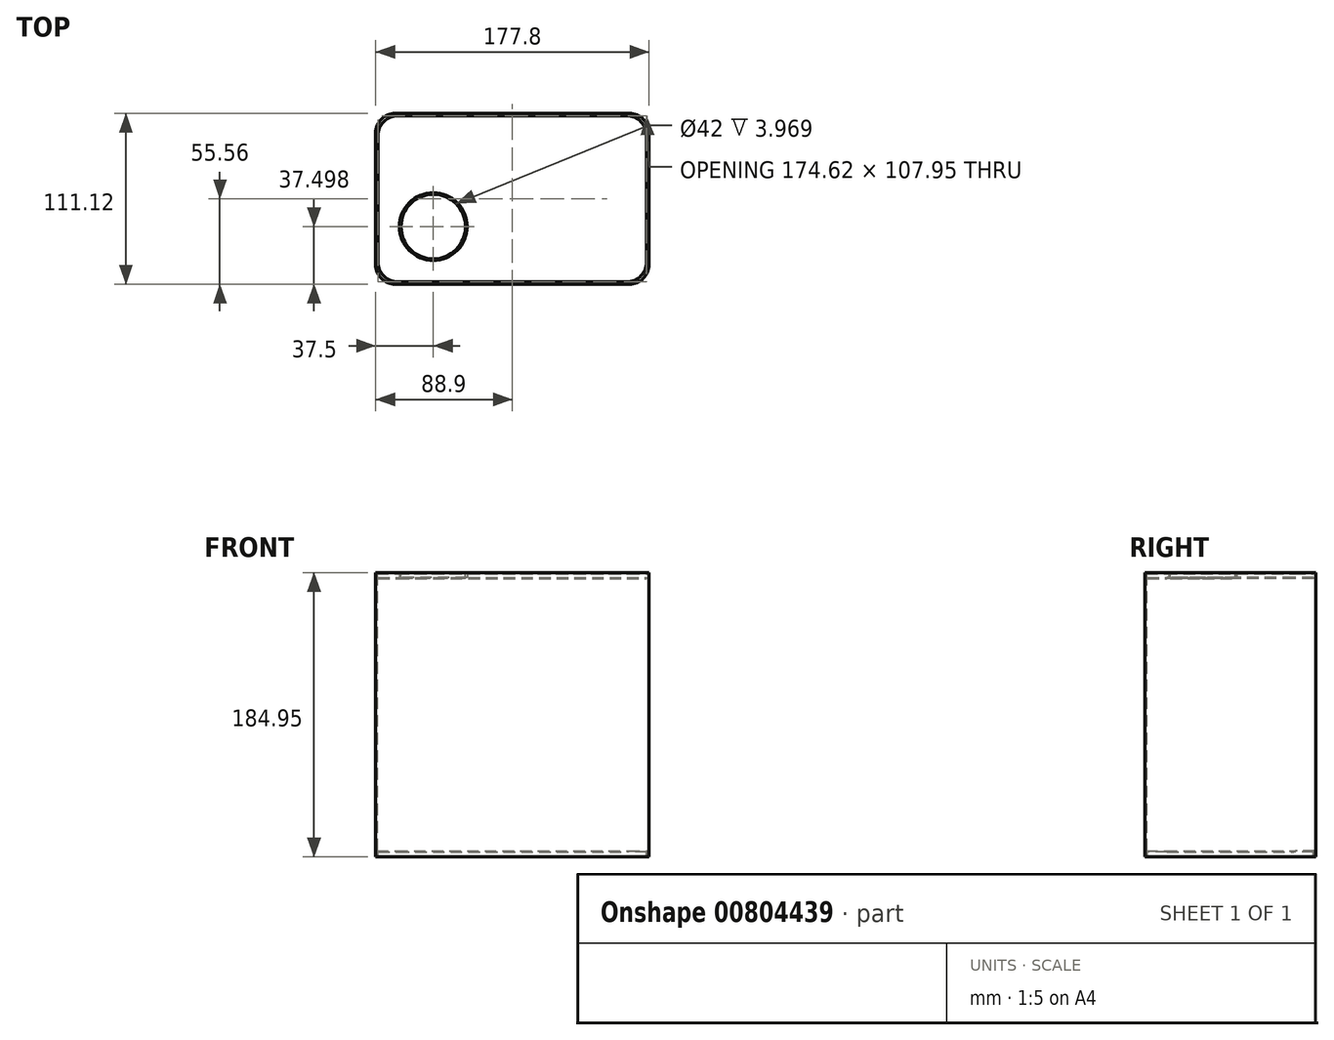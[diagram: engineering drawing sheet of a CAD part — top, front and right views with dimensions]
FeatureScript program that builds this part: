
annotation { "Feature Type Name" : "Feature", "Feature Type Description" : "" }
export const myFeature = defineFeature(function(context is Context, id is Id, definition is map)
    precondition{}
    {
        {
            var Q0;
            Q0=qCreatedBy(makeId("Top.planeOp"),FACE);
            var sketch = newSketch(context, id + "F0", { "sketchPlane" : qUnion([Q0])});
            skLineSegment(sketch, "E0.bottom", {"start": v(-76.2, -55.56) * mm, "end": v(76.2, -55.56) * mm});
            skLineSegment(sketch, "E0.top", {"start": v(-76.2, 55.56) * mm, "end": v(76.2, 55.56) * mm});
            skLineSegment(sketch, "E0.left", {"start": v(-88.9, -42.86) * mm, "end": v(-88.9, 42.86) * mm});
            skLineSegment(sketch, "E0.right", {"start": v(88.9, -42.86) * mm, "end": v(88.9, 42.86) * mm});
            skPoint(sketch, "E0.middle", {"position": v(0, 0) * mm});
            skPoint(sketch, "E1.visualSharp", {"position": v(-88.9, -55.56) * mm});
            skArc(sketch, "E1.filletArc", {"start": v(-88.9, -42.86) * mm, "mid": v(-85.18, -51.84) * mm, "end": v(-76.2, -55.56) * mm});
            skPoint(sketch, "E2.visualSharp", {"position": v(-88.9, 55.56) * mm});
            skArc(sketch, "E2.filletArc", {"start": v(-76.2, 55.56) * mm, "mid": v(-85.18, 51.84) * mm, "end": v(-88.9, 42.86) * mm});
            skPoint(sketch, "E3.visualSharp", {"position": v(88.9, 55.56) * mm});
            skArc(sketch, "E3.filletArc", {"start": v(88.9, 42.86) * mm, "mid": v(85.18, 51.84) * mm, "end": v(76.2, 55.56) * mm});
            skPoint(sketch, "E4.visualSharp", {"position": v(88.9, -55.56) * mm});
            skArc(sketch, "E4.filletArc", {"start": v(76.2, -55.56) * mm, "mid": v(85.18, -51.84) * mm, "end": v(88.9, -42.86) * mm});
            skSolve(sketch);
        }
        {
            var Q0;
            Q0 = qSketchRegion(id + "F0", true);
            extrude(context, id + "F1", {"entities" : qUnion([Q0]), "endBound" : BoundingType.SYMMETRIC, "depth" : 180.97 * mm, "offsetDistance" : 25.4 * mm});
        }
        {
            var Q0;
            Q0=makeQuery(id+"F1.opExtrude","CAP_FACE",FACE,{"disambiguationData":[OSD([sQuery(id+"F0.wireOp",EDGE,"E0.bottom"),sQuery(id+"F0.wireOp",EDGE,"E0.top"),sQuery(id+"F0.wireOp",EDGE,"E0.left"),sQuery(id+"F0.wireOp",EDGE,"E0.right"),sQuery(id+"F0.wireOp",EDGE,"E1.filletArc"),sQuery(id+"F0.wireOp",EDGE,"E2.filletArc"),sQuery(id+"F0.wireOp",EDGE,"E3.filletArc"),sQuery(id+"F0.wireOp",EDGE,"E4.filletArc")])],"isStart":false});
            var sketch = newSketch(context, id + "F2", { "sketchPlane" : qUnion([Q0])});
            skLineSegment(sketch, "E5.bottom", {"start": v(-74.61, 53.98) * mm, "end": v(74.61, 53.98) * mm});
            skLineSegment(sketch, "E5.top", {"start": v(-74.61, -53.98) * mm, "end": v(74.61, -53.98) * mm});
            skLineSegment(sketch, "E5.left", {"start": v(-87.31, 41.27) * mm, "end": v(-87.31, -41.28) * mm});
            skLineSegment(sketch, "E5.right", {"start": v(87.31, 41.28) * mm, "end": v(87.31, -41.27) * mm});
            skPoint(sketch, "E5.middle", {"position": v(0, 0) * mm});
            skPoint(sketch, "E6.visualSharp", {"position": v(-87.31, 53.98) * mm});
            skArc(sketch, "E6.filletArc", {"start": v(-74.61, 53.98) * mm, "mid": v(-83.6, 50.26) * mm, "end": v(-87.31, 41.27) * mm});
            skPoint(sketch, "E7.visualSharp", {"position": v(87.31, 53.98) * mm});
            skArc(sketch, "E7.filletArc", {"start": v(87.31, 41.28) * mm, "mid": v(83.6, 50.26) * mm, "end": v(74.61, 53.97) * mm});
            skPoint(sketch, "E8.visualSharp", {"position": v(87.31, -53.98) * mm});
            skArc(sketch, "E8.filletArc", {"start": v(74.61, -53.98) * mm, "mid": v(83.6, -50.26) * mm, "end": v(87.31, -41.27) * mm});
            skPoint(sketch, "E9.visualSharp", {"position": v(-87.31, -53.98) * mm});
            skArc(sketch, "E9.filletArc", {"start": v(-87.31, -41.28) * mm, "mid": v(-83.6, -50.26) * mm, "end": v(-74.61, -53.98) * mm});
            skSolve(sketch);
        }
        {
            var Q0;
            Q0=makeQuery(id+"F2.imprint","IMPRINT",FACE,{"disambiguationData":[TD([[makeQuery(id+"F2.imprint","IMPRINT",EDGE,{"derivedFrom":sQuery(id+"F2.wireOp",EDGE,"E5.bottom")}),-1.0]])]});
            extrude(context, id + "F3", {"entities" : qUnion([Q0]), "operationType" : NewBodyOperationType.REMOVE, "oppositeDirection" : true, "depth" : 3.17 * mm, "offsetDistance" : 25.4 * mm});
        }
        {
            var Q0;
            Q0=makeQuery(id+"F1.opExtrude","CAP_FACE",FACE,{"disambiguationData":[OSD([sQuery(id+"F0.wireOp",EDGE,"E0.bottom"),sQuery(id+"F0.wireOp",EDGE,"E0.top"),sQuery(id+"F0.wireOp",EDGE,"E0.left"),sQuery(id+"F0.wireOp",EDGE,"E0.right"),sQuery(id+"F0.wireOp",EDGE,"E1.filletArc"),sQuery(id+"F0.wireOp",EDGE,"E2.filletArc"),sQuery(id+"F0.wireOp",EDGE,"E3.filletArc"),sQuery(id+"F0.wireOp",EDGE,"E4.filletArc")])],"isStart":true});
            var sketch = newSketch(context, id + "F4", { "sketchPlane" : qUnion([Q0])});
            skLineSegment(sketch, "E10.bottom", {"start": v(-75.4, 54.77) * mm, "end": v(75.4, 54.77) * mm});
            skLineSegment(sketch, "E10.top", {"start": v(-75.4, -54.77) * mm, "end": v(75.4, -54.77) * mm});
            skLineSegment(sketch, "E10.left", {"start": v(-88.1, 42.07) * mm, "end": v(-88.1, -42.07) * mm});
            skLineSegment(sketch, "E10.right", {"start": v(88.1, 42.07) * mm, "end": v(88.1, -42.07) * mm});
            skPoint(sketch, "E10.middle", {"position": v(0, 0) * mm});
            skPoint(sketch, "E11.visualSharp", {"position": v(-88.1, 54.77) * mm});
            skArc(sketch, "E11.filletArc", {"start": v(-75.4, 54.77) * mm, "mid": v(-84.39, 51.05) * mm, "end": v(-88.1, 42.07) * mm});
            skPoint(sketch, "E12.visualSharp", {"position": v(88.1, 54.77) * mm});
            skArc(sketch, "E12.filletArc", {"start": v(88.1, 42.07) * mm, "mid": v(84.39, 51.05) * mm, "end": v(75.4, 54.77) * mm});
            skPoint(sketch, "E13.visualSharp", {"position": v(88.1, -54.77) * mm});
            skArc(sketch, "E13.filletArc", {"start": v(75.4, -54.77) * mm, "mid": v(84.39, -51.05) * mm, "end": v(88.1, -42.07) * mm});
            skPoint(sketch, "E14.visualSharp", {"position": v(-88.1, -54.77) * mm});
            skArc(sketch, "E14.filletArc", {"start": v(-88.1, -42.07) * mm, "mid": v(-84.39, -51.05) * mm, "end": v(-75.4, -54.77) * mm});
            skSolve(sketch);
        }
        {
            var Q0;
            Q0=makeQuery(id+"F4.imprint","IMPRINT",FACE,{"disambiguationData":[TD([[makeQuery(id+"F4.imprint","IMPRINT",EDGE,{"derivedFrom":sQuery(id+"F4.wireOp",EDGE,"E10.bottom")}),-1.0]])]});
            extrude(context, id + "F5", {"entities" : qUnion([Q0]), "operationType" : NewBodyOperationType.REMOVE, "endBound" : BoundingType.UP_TO_NEXT, "oppositeDirection" : true, "depth" : 25.4 * mm, "hasOffset" : true, "offsetDistance" : 0.8 * mm});
        }
        {
            var Q0;
            Q0=makeQuery(id+"F1.opExtrude","CAP_FACE",FACE,{"disambiguationData":[OSD([sQuery(id+"F0.wireOp",EDGE,"E0.bottom"),sQuery(id+"F0.wireOp",EDGE,"E0.top"),sQuery(id+"F0.wireOp",EDGE,"E0.left"),sQuery(id+"F0.wireOp",EDGE,"E0.right"),sQuery(id+"F0.wireOp",EDGE,"E1.filletArc"),sQuery(id+"F0.wireOp",EDGE,"E2.filletArc"),sQuery(id+"F0.wireOp",EDGE,"E3.filletArc"),sQuery(id+"F0.wireOp",EDGE,"E4.filletArc")])],"isStart":true});
            var sketch = newSketch(context, id + "F6", { "sketchPlane" : qUnion([Q0])});
            skLineSegment(sketch, "E15.bottom", {"start": v(-76.2, 55.56) * mm, "end": v(76.2, 55.56) * mm});
            skLineSegment(sketch, "E15.top", {"start": v(-76.2, -55.56) * mm, "end": v(76.2, -55.56) * mm});
            skLineSegment(sketch, "E15.left", {"start": v(-88.9, 42.86) * mm, "end": v(-88.9, -42.86) * mm});
            skLineSegment(sketch, "E15.right", {"start": v(88.9, 42.86) * mm, "end": v(88.9, -42.86) * mm});
            skPoint(sketch, "E15.middle", {"position": v(0, 0) * mm});
            skPoint(sketch, "E16.visualSharp", {"position": v(-88.9, 55.56) * mm});
            skArc(sketch, "E16.filletArc", {"start": v(-76.2, 55.56) * mm, "mid": v(-85.18, 51.84) * mm, "end": v(-88.9, 42.86) * mm});
            skPoint(sketch, "E17.visualSharp", {"position": v(88.9, 55.56) * mm});
            skArc(sketch, "E17.filletArc", {"start": v(88.9, 42.86) * mm, "mid": v(85.18, 51.84) * mm, "end": v(76.2, 55.56) * mm});
            skPoint(sketch, "E18.visualSharp", {"position": v(88.9, -55.56) * mm});
            skArc(sketch, "E18.filletArc", {"start": v(76.2, -55.56) * mm, "mid": v(85.18, -51.84) * mm, "end": v(88.9, -42.86) * mm});
            skPoint(sketch, "E19.visualSharp", {"position": v(-88.9, -55.56) * mm});
            skArc(sketch, "E19.filletArc", {"start": v(-88.9, -42.86) * mm, "mid": v(-85.18, -51.84) * mm, "end": v(-76.2, -55.56) * mm});
            skSolve(sketch);
        }
        {
            var Q0;
            Q0 = qSketchRegion(id + "F6", true);
            extrude(context, id + "F7", {"entities" : qUnion([Q0]), "operationType" : NewBodyOperationType.ADD, "depth" : 0.8 * mm, "offsetDistance" : 25.4 * mm});
        }
        {
            var Q0;
            Q0=makeQuery(id+"F7.opExtrude","CAP_FACE",FACE,{"disambiguationData":[OSD([sQuery(id+"F6.wireOp",EDGE,"E15.bottom"),sQuery(id+"F6.wireOp",EDGE,"E15.top"),sQuery(id+"F6.wireOp",EDGE,"E15.left"),sQuery(id+"F6.wireOp",EDGE,"E15.right"),sQuery(id+"F6.wireOp",EDGE,"E16.filletArc"),sQuery(id+"F6.wireOp",EDGE,"E17.filletArc"),sQuery(id+"F6.wireOp",EDGE,"E18.filletArc"),sQuery(id+"F6.wireOp",EDGE,"E19.filletArc")])],"isStart":false});
            var sketch = newSketch(context, id + "F8", { "sketchPlane" : qUnion([Q0])});
            skLineSegment(sketch, "E20.bottom", {"start": v(-76.2, 55.56) * mm, "end": v(76.2, 55.56) * mm});
            skLineSegment(sketch, "E20.top", {"start": v(-76.2, -55.56) * mm, "end": v(76.2, -55.56) * mm});
            skLineSegment(sketch, "E20.left", {"start": v(-88.9, 42.86) * mm, "end": v(-88.9, -42.86) * mm});
            skLineSegment(sketch, "E20.right", {"start": v(88.9, 42.86) * mm, "end": v(88.9, -42.86) * mm});
            skPoint(sketch, "E20.middle", {"position": v(0, 0) * mm});
            skPoint(sketch, "E21.visualSharp", {"position": v(-88.9, 55.56) * mm});
            skArc(sketch, "E21.filletArc", {"start": v(-76.2, 55.56) * mm, "mid": v(-85.18, 51.84) * mm, "end": v(-88.9, 42.86) * mm});
            skPoint(sketch, "E22.visualSharp", {"position": v(-88.9, -55.56) * mm});
            skArc(sketch, "E22.filletArc", {"start": v(-88.9, -42.86) * mm, "mid": v(-85.18, -51.84) * mm, "end": v(-76.2, -55.56) * mm});
            skPoint(sketch, "E23.visualSharp", {"position": v(88.9, -55.56) * mm});
            skArc(sketch, "E23.filletArc", {"start": v(76.2, -55.56) * mm, "mid": v(85.18, -51.84) * mm, "end": v(88.9, -42.86) * mm});
            skPoint(sketch, "E24.visualSharp", {"position": v(88.9, 55.56) * mm});
            skArc(sketch, "E24.filletArc", {"start": v(88.9, 42.86) * mm, "mid": v(85.18, 51.84) * mm, "end": v(76.2, 55.56) * mm});
            skLineSegment(sketch, "E25.bottom", {"start": v(-74.61, 53.97) * mm, "end": v(74.61, 53.97) * mm});
            skLineSegment(sketch, "E25.top", {"start": v(-74.61, -53.97) * mm, "end": v(74.61, -53.97) * mm});
            skLineSegment(sketch, "E25.left", {"start": v(-87.31, 41.27) * mm, "end": v(-87.31, -41.27) * mm});
            skLineSegment(sketch, "E25.right", {"start": v(87.31, 41.27) * mm, "end": v(87.31, -41.27) * mm});
            skPoint(sketch, "E26.visualSharp", {"position": v(-87.31, 53.98) * mm});
            skArc(sketch, "E26.filletArc", {"start": v(-74.61, 53.97) * mm, "mid": v(-83.6, 50.26) * mm, "end": v(-87.31, 41.27) * mm});
            skPoint(sketch, "E27.visualSharp", {"position": v(87.31, 53.97) * mm});
            skArc(sketch, "E27.filletArc", {"start": v(87.31, 41.27) * mm, "mid": v(83.6, 50.26) * mm, "end": v(74.61, 53.97) * mm});
            skPoint(sketch, "E28.visualSharp", {"position": v(87.31, -53.98) * mm});
            skArc(sketch, "E28.filletArc", {"start": v(74.61, -53.97) * mm, "mid": v(83.6, -50.26) * mm, "end": v(87.31, -41.27) * mm});
            skPoint(sketch, "E29.visualSharp", {"position": v(-87.31, -53.97) * mm});
            skArc(sketch, "E29.filletArc", {"start": v(-87.31, -41.27) * mm, "mid": v(-83.6, -50.26) * mm, "end": v(-74.61, -53.97) * mm});
            skSolve(sketch);
        }
        {
            var Q0;
            Q0 = qSketchRegion(id + "F8", true);
            extrude(context, id + "F9", {"entities" : qUnion([Q0]), "operationType" : NewBodyOperationType.ADD, "depth" : 3.17 * mm, "offsetDistance" : 25.4 * mm});
        }
        {
            var Q0;
            Q0=makeQuery(id+"F3.boolean.opBoolean","COPY",FACE,{"derivedFrom":makeQuery(id+"F3.opExtrude","CAP_FACE",FACE,{"disambiguationData":[OSD([sQuery(id+"F2.wireOp",EDGE,"E5.bottom"),sQuery(id+"F2.wireOp",EDGE,"E5.top"),sQuery(id+"F2.wireOp",EDGE,"E5.left"),sQuery(id+"F2.wireOp",EDGE,"E5.right"),sQuery(id+"F2.wireOp",EDGE,"E6.filletArc"),sQuery(id+"F2.wireOp",EDGE,"E7.filletArc"),sQuery(id+"F2.wireOp",EDGE,"E8.filletArc"),sQuery(id+"F2.wireOp",EDGE,"E9.filletArc")])],"isStart":false})});
            var sketch = newSketch(context, id + "F10", { "sketchPlane" : qUnion([Q0])});
            skCircle(sketch, "E30", {"center": v(-51.4, -18.06) * mm, "radius": 21 * mm});
            skSolve(sketch);
        }
        {
            var Q0;
            Q0=makeQuery(id+"F10.imprint","IMPRINT",FACE,{"disambiguationData":[TD([[makeQuery(id+"F10.imprint","IMPRINT",EDGE,{"derivedFrom":sQuery(id+"F10.wireOp",EDGE,"E30")}),1.0]])]});
            extrude(context, id + "F11", {"entities" : qUnion([Q0]), "operationType" : NewBodyOperationType.REMOVE, "oppositeDirection" : true, "depth" : 25.4 * mm, "offsetDistance" : 25.4 * mm});
        }
        {
            var Q0;
            Q0=makeQuery(id+"F3.boolean.opBoolean","COPY",FACE,{"derivedFrom":makeQuery(id+"F3.opExtrude","CAP_FACE",FACE,{"disambiguationData":[OSD([sQuery(id+"F2.wireOp",EDGE,"E5.bottom"),sQuery(id+"F2.wireOp",EDGE,"E5.top"),sQuery(id+"F2.wireOp",EDGE,"E5.left"),sQuery(id+"F2.wireOp",EDGE,"E5.right"),sQuery(id+"F2.wireOp",EDGE,"E6.filletArc"),sQuery(id+"F2.wireOp",EDGE,"E7.filletArc"),sQuery(id+"F2.wireOp",EDGE,"E8.filletArc"),sQuery(id+"F2.wireOp",EDGE,"E9.filletArc")])],"isStart":false})});
            var sketch = newSketch(context, id + "F12", { "sketchPlane" : qUnion([Q0])});
            skCircle(sketch, "E31", {"center": v(-51.4, -18.06) * mm, "radius": 22 * mm});
            skSolve(sketch);
        }
        {
            var Q0;
            Q0=makeQuery(id+"F12.imprint","IMPRINT",FACE,{"disambiguationData":[TD([[makeQuery(id+"F12.imprint","IMPRINT",EDGE,{"derivedFrom":sQuery(id+"F12.wireOp",EDGE,"E31")}),1.0]])]});
            extrude(context, id + "F13", {"entities" : qUnion([Q0]), "operationType" : NewBodyOperationType.ADD, "depth" : 3.17 * mm, "offsetDistance" : 25.4 * mm});
        }
    });
